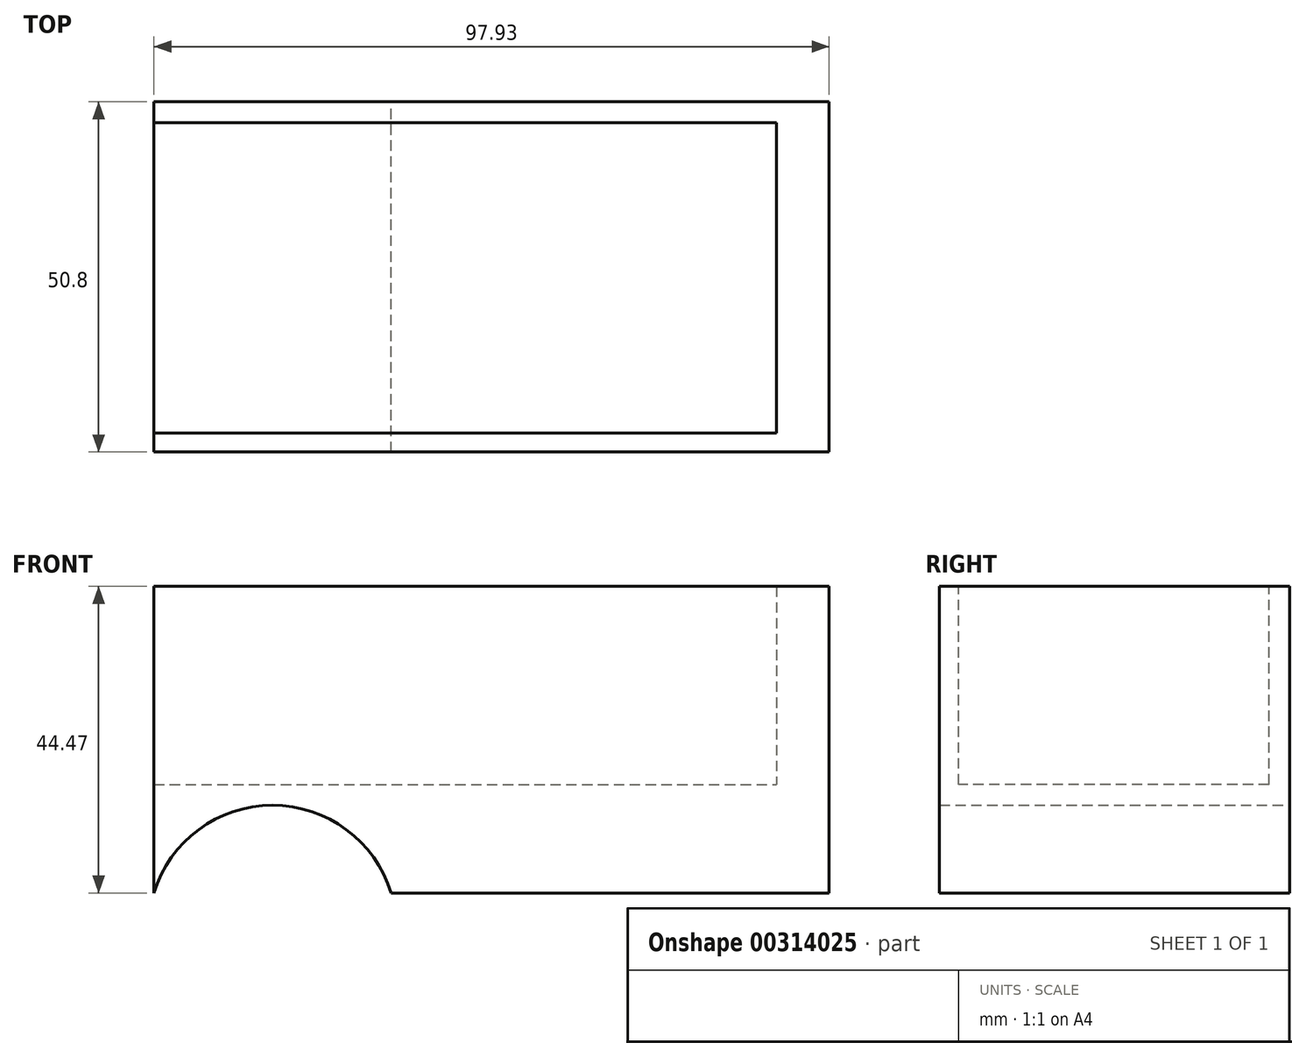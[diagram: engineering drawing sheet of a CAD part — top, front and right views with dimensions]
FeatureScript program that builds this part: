
annotation { "Feature Type Name" : "Feature", "Feature Type Description" : "" }
export const myFeature = defineFeature(function(context is Context, id is Id, definition is map)
    precondition{}
    {
        {
            var Q0;
            Q0=qCreatedBy(makeId("Front.planeOp"),FACE);
            var sketch = newSketch(context, id + "F0", { "sketchPlane" : qUnion([Q0])});
            skLineSegment(sketch, "E0", {"start": v(38.18, 0) * mm, "end": v(38.18, 44.47) * mm});
            skLineSegment(sketch, "E1", {"start": v(38.18, 44.47) * mm, "end": v(-59.75, 44.47) * mm});
            skLineSegment(sketch, "E2", {"start": v(-59.75, 44.47) * mm, "end": v(-59.75, 0) * mm});
            skLineSegment(sketch, "E3", {"start": v(38.18, 0) * mm, "end": v(-25.36, 0) * mm});
            skArc(sketch, "E4", {"start": v(-25.36, 0) * mm, "mid": v(-42.56, 12.72) * mm, "end": v(-59.75, 0) * mm});
            skSolve(sketch);
        }
        {
            var Q0;
            Q0=makeQuery(id+"F0.imprint","IMPRINT",FACE,{"disambiguationData":[TD([[makeQuery(id+"F0.imprint","IMPRINT",EDGE,{"derivedFrom":sQuery(id+"F0.wireOp",EDGE,"E0")}),1.0]])]});
            extrude(context, id + "F1", {"entities" : qUnion([Q0]), "depth" : 50.8 * mm});
        }
        {
            var Q0;
            Q0=qCreatedBy(makeId("Top.planeOp"),FACE);
            var sketch = newSketch(context, id + "F2", { "sketchPlane" : qUnion([Q0])});
            skLineSegment(sketch, "E5.bottom", {"start": v(-62.9, -48.05) * mm, "end": v(30.55, -48.05) * mm});
            skLineSegment(sketch, "E5.top", {"start": v(-62.9, -3) * mm, "end": v(30.55, -3) * mm});
            skLineSegment(sketch, "E5.left", {"start": v(-62.9, -48.05) * mm, "end": v(-62.9, -3) * mm});
            skLineSegment(sketch, "E5.right", {"start": v(30.55, -48.05) * mm, "end": v(30.55, -3) * mm});
            skSolve(sketch);
        }
        {
            var Q0;
            Q0 = qSketchRegion(id + "F2", true);
            extrude(context, id + "F3", {"entities" : qUnion([Q0]), "operationType" : NewBodyOperationType.REMOVE, "depth" : 65.8 * mm, "hasSecondDirection" : true, "secondDirectionOppositeDirection" : false, "secondDirectionDepth" : 15.75 * mm});
        }
    });
